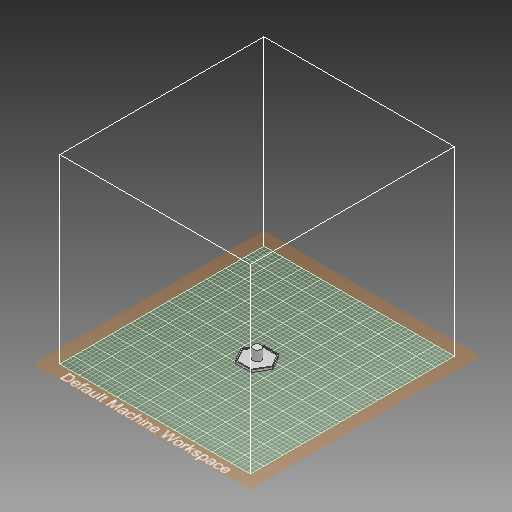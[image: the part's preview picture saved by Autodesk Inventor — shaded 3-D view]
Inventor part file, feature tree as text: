
AUTODESK INVENTOR PART (.ipt)
format: ipt  version: 2019 (Build 230136000, 136)  size: 374,272 bytes
history: native  units: mm
features: extrude x4, sketch x1
ambient origin geometry x8: Origin, YZ Plane, XZ Plane, XY Plane, X Axis, Y Axis, Z Axis, Center Point
bodies: Solid1 (feature_tree)
feature tree (5):
  sketch  "Sketch1"  dims[d0=70.0mm d1=2.0mm d2=17.5mm d3=3.0mm d4=0.0mm d5=5.0mm d7=5.0mm d8=0.0mm d9=40.0mm d10=0.0mm d15=1.0mm d16=0.0mm]
  extrude  "Extrusion1"  Depth=2.0mm
  extrude  "Extrusion3"  Depth=17.5mm
  extrude  "Extrusion4"  Depth=3.0mm TaperAngle=0.0deg
  extrude  "Extrusion6"  Depth=5.0mm TaperAngle=0.0deg
